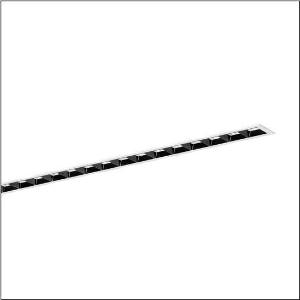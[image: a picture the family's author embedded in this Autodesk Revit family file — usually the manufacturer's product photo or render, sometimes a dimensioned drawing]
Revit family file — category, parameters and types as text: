
# Revit family: silica_r__21_51mx12tctaw_2b1a
name_source: partatom
category: Lighting Fixtures
units: mm (PartAtom-declared; Revit-internal decimal feet)

## family parameters
Cut with Voids When Loaded = No
Host = Face
Light Source = No
Part Type = Normal
Room Calculation Point = No
Round Connector Dimension = Use Diameter
Shared = No

## types (1)
- --- (1 x LED, 9300 lm, 80.4 W, 6500K)
    Apparent Load = 80 VA
    CIE Flux Codes = 84 100 100 100 100
    Color Rendering = 80
    Color Temperature = 6500K
    Default Elevation = 1800 mm
    Description = Silica® 21, office luminaire, primary light control with darklight reflector, of PMMA, black, CAT 2 (L<= 3000cd/m²), light emission: direct distribution, primary light characteristic: symmetric, installation type: recessed, LED, rated luminous flux: 9.300lm, luminous efficacy: 110lm/W, light colour: 8tw, colour temperature: 2700..6500K, with terminal, 3+2-pole, max. 2.5mm², mains connection: 220..240V, AC, 50/60Hz, rated input power: 84.5W, luminaire housing, of aluminium, traffic white (RAL 9016), length: 3.028mm, width: 79mm, height: 53mm, protection rating (complete): IP20, insulation class (complete): insulation class I (protective earthing), certification: CE, permissible operating ambient temperature: 0..+35°C, standard: EN 50419, packaging unit: 1 piece
    Height = 0 mm  [stored 0 ft]
    Lamp = 1 x LED
    Lamp Light Flux = 9300 lm
    Lamp Power = 80.4 W
    Lamp count = 1
    Length = 3027 mm
    Luminous efficacy = 116 lm/W
    Manufacturer = Siteco
    ModVariant = No
    Model = 51MX12TCTAW
    Mounting Place = Ceiling
    Mounting Type = Recessed
    Number of Poles = 1
    OnlyDefault = Yes
    Power Factor = 1
    Product Name = Silica® 21
    Product group = office luminaire | ceiling recessed
    ProductGroupID = 401
    Protection Class = Protection class I
    Protection Degree = IP 20
    RLX_Detail_Level = 1
    RLX_Emergency_Light_Flux = 0 lm
    RLX_Emergency_Type = 0
    RLX_Emergency_Type_DB = No
    RlxData = <blob elided: 60217 chars, md5=1d3418f6>
    Socket = socket
    Standby Power = 0 W
    System Light Flux = 9300 lm
    System Power = 80 W
    Type Comments = individual setting
    Type Image = l_1297791.jpg
    URL = http://relux.com
    VarID = @adj_071491
    Voltage = 0 V
    Weight = 0.00 kg
    Width = 79 mm

note: [stored X ft] marks values corroborated as IEEE doubles in the binary element streams (Revit-internal decimal feet)

## geometry (parser evidence)
native form markers: Blend x4, Sweep x13
no freeform markers — native parametric forms only
